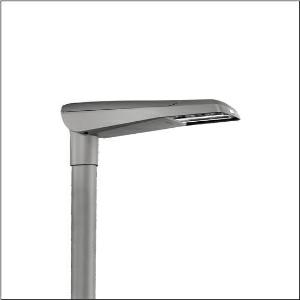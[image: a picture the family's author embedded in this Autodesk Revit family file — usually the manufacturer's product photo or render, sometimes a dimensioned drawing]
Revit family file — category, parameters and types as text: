
# Revit family: streetlight_sl_11_iq_micro___st1_0ab_5xc1n41f08ce_2768
name_source: partatom
category: Lighting Fixtures
units: mm (PartAtom-declared; Revit-internal decimal feet)

## family parameters
Cut with Voids When Loaded = No
Host = Face
Light Source = No
Part Type = Normal
Room Calculation Point = No
Round Connector Dimension = Use Diameter
Shared = No

## types (1)
- --- (1 x LED, 1650 lm, 12.6 W, 4000K)
    Apparent Load = 13 VA
    CIE Flux Codes = 29 63 95 100 100
    Color Rendering = 70
    Color Temperature = 4000K
    Default Elevation = 1800 mm
    Description = Streetlight SL 11 iQ micro, mast luminaire, primary light control with 3 zone facetted reflector, of plastic, silver coated, highly specular, primary optical cover: cover, of PMMA, transparent, light distribution: ST1.0aB, light emission: direct distribution, primary light characteristic: asymmetric, installation type: post-top, side-entry, lamps: LED, High Power LED, rated values: 1.650lm | 12,6W | 131lm/W (begin service life); end service life: 1.650lm | 12,9W; at 50% lumin. flux: 825lm | 6,8W | 121,3lm/W, colour temperature: 4000K, colour rendering: CRI > 70, light colour: 740, light setting 1 begin service life: 100% | 1.650lm | 12,6W | 131lm/W | 4.000K, light setting 1 end service life: 12,9W, further light settings possible, control: optimised constant luminous flux control (CLO 2.0), Desk-Remote (wireless, voltage-free reading and setting of iQ features in the workshop via application-optimized NFC function/RFID function), Light-Fading, Smart-Wire, Night-Set, Lumen-Switch, Temp-Guard, Auto-Match, Street-Remote, with cable H07RN-F 3x 1.5mm², mains connection: 230..240V, AC, 50/60Hz, connection cable pre-assembled, cable length: 5,5m, luminaire housing, of diecast aluminium, powder-coated, SITECO metallic grey (DB 702S), please order mast flange separately, inclination adjustable without tools: 0°, 5°, 10°, 15° (post-top) | 0°, -5°, -10°, -15° (side-entry), sealing non-destructively replaceable, multi-level sealing system, length: 600mm, width: 174mm, height: 116mm, mast flange for spigot size: 42mm (side-entry): 5XC10008XM4, 60/48mm (side-entry/post-top): 5XC10108XM2, 76/60mm (side-entry/post-top): 5XC10108XM1, equipment: standard, protection rating (complete): IP66, insulation class (complete): insulation class II (safety insulation), certification: CE, ENEC, ENEC+, VDE, impact resistance: IK10, permissible operating ambient temperature for outdoor applications: -25..+50°C, standard-compliant lighting for roads and squares, Environmental Product Declaration (EPD) tested and certified by an independent institute, packaging unit: 1 piece

Light Distribution: ST1.0aB
    Height = 116 mm
    Lamp = 1 x LED
    Lamp Light Flux = 1650 lm
    Lamp Power = 12.6 W
    Lamp count = 1
    Length = 600 mm
    Luminous efficacy = 131 lm/W
    Manufacturer = Siteco
    ModVariant = No
    Model = 5XC1N41F08CE
    Mounting Place = Pole
    Mounting Type = Pole top
    Number of Poles = 1
    OnlyDefault = Yes
    Power Factor = 1
    Product Name = Streetlight SL 11 iQ micro | ST1.0aB
    Product group = mast luminaire | pylon top
    ProductGroupID = 6100
    Protection Class = Protection class II
    Protection Degree = IP 66
    RLX_Detail_Level = 1
    RLX_Emergency_Light_Flux = 0 lm
    RLX_Emergency_Type = 0
    RLX_Emergency_Type_DB = No
    RlxData = <blob elided: 26317 chars, md5=dc4dc8af>
    Socket = socket
    Standby Power = 0 W
    System Light Flux = 1650 lm
    System Power = 13 W
    Type Comments = factory setting: luminous flux: 100 % | dim-lin: 254 | 229 mA
    Type Image = l_1006566.jpg
    URL = http://relux.com
    VarID = @adj_022487
    Voltage = 0 V
    Weight = 0.00 kg
    Width = 174 mm

## geometry (parser evidence)
native form markers: Blend x4, Sweep x10
no freeform markers — native parametric forms only
